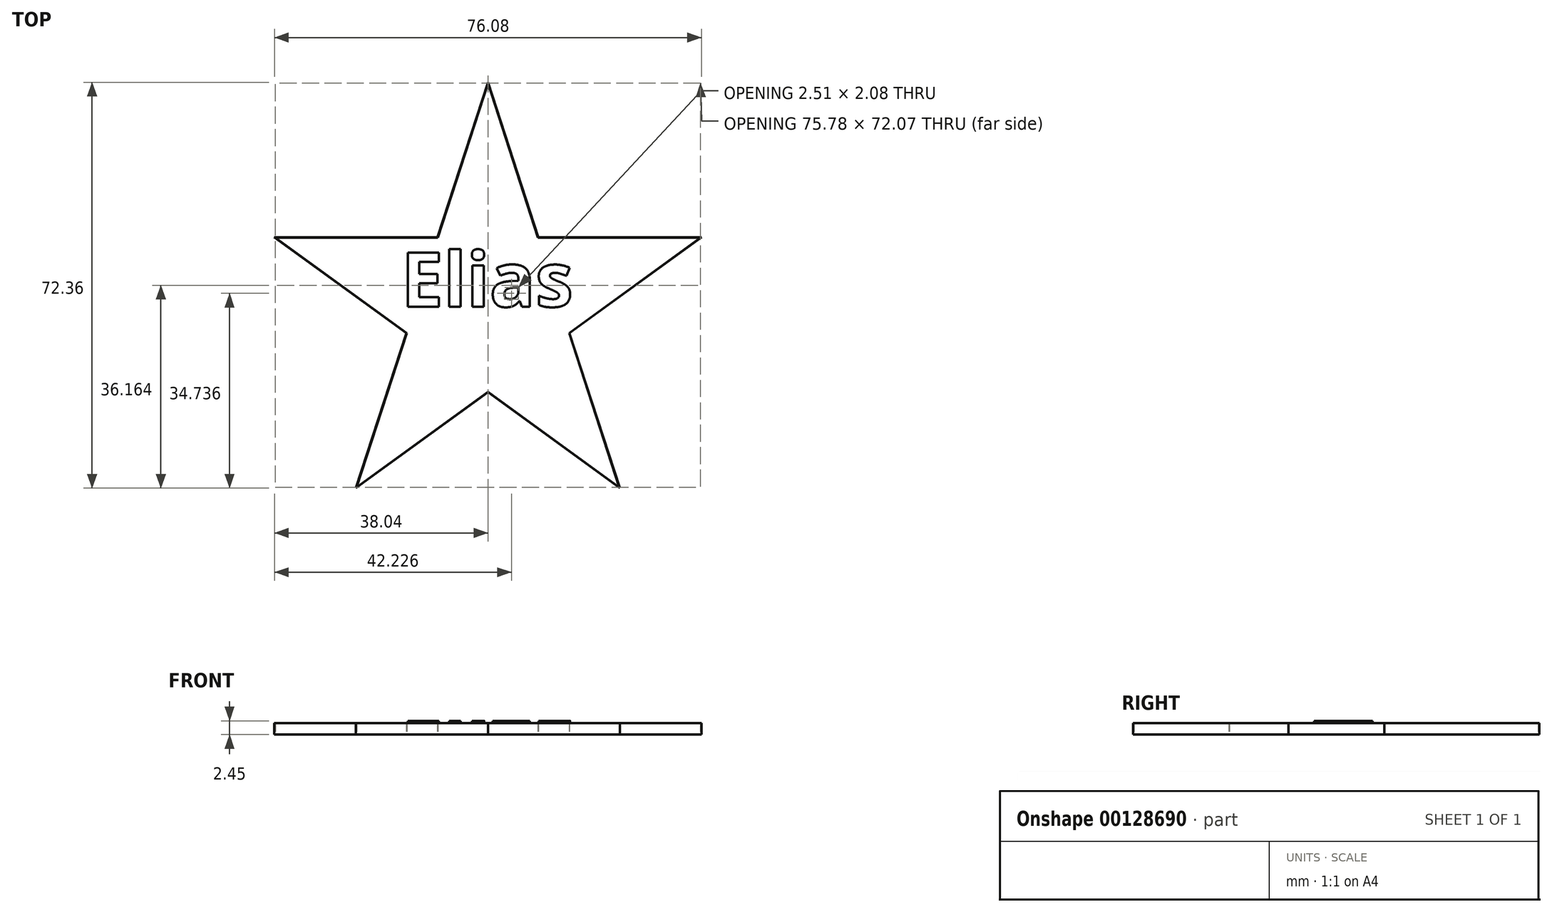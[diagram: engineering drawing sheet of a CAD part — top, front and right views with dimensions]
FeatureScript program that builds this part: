
annotation { "Feature Type Name" : "Feature", "Feature Type Description" : "" }
export const myFeature = defineFeature(function(context is Context, id is Id, definition is map)
    precondition{}
    {
        {
            assignVariable(context, id + "F0", {"name" : "Thickness", "anyValue" : 2 * mm});
        }
        {
            var Q0;
            Q0=qCreatedBy(makeId("Top.planeOp"),FACE);
            var sketch = newSketch(context, id + "F1", { "sketchPlane" : qUnion([Q0])});
            skLineSegment(sketch, "E0", {"start": v(0, 0) * mm, "end": v(0, 40) * mm, "construction": true});
            skLineSegment(sketch, "E1", {"start": v(0, 40) * mm, "end": v(-13, 0) * mm, "construction": true});
            skLineSegment(sketch, "E2", {"start": v(-13, 0) * mm, "end": v(13, 0) * mm, "construction": true});
            skLineSegment(sketch, "E3", {"start": v(0, 40) * mm, "end": v(13, 0) * mm, "construction": true});
            skPoint(sketch, "E4.center", {"position": v(0, 0) * mm});
            skLineSegment(sketch, "E5.1.0", {"start": v(-38.04, 12.36) * mm, "end": v(-4.02, -12.36) * mm, "construction": true});
            skLineSegment(sketch, "E5.1.1", {"start": v(-38.04, 12.36) * mm, "end": v(4.02, 12.36) * mm, "construction": true});
            skLineSegment(sketch, "E5.2.0", {"start": v(-23.51, -32.36) * mm, "end": v(10.51, -7.64) * mm, "construction": true});
            skLineSegment(sketch, "E5.2.1", {"start": v(-23.51, -32.36) * mm, "end": v(-10.51, 7.64) * mm, "construction": true});
            skLineSegment(sketch, "E5.3.0", {"start": v(23.51, -32.36) * mm, "end": v(10.51, 7.64) * mm, "construction": true});
            skLineSegment(sketch, "E5.3.1", {"start": v(23.51, -32.36) * mm, "end": v(-10.51, -7.64) * mm, "construction": true});
            skLineSegment(sketch, "E5.4.0", {"start": v(38.04, 12.36) * mm, "end": v(-4.02, 12.36) * mm, "construction": true});
            skLineSegment(sketch, "E5.4.1", {"start": v(38.04, 12.36) * mm, "end": v(4.02, -12.36) * mm, "construction": true});
            skPoint(sketch, "E6", {"position": v(-8.98, 12.36) * mm});
            skPoint(sketch, "E7", {"position": v(8.98, 12.36) * mm});
            skPoint(sketch, "E8", {"position": v(14.53, -4.72) * mm});
            skPoint(sketch, "E9", {"position": v(0, -15.28) * mm});
            skPoint(sketch, "E10", {"position": v(-14.53, -4.72) * mm});
            skLineSegment(sketch, "E11", {"start": v(0, 40) * mm, "end": v(8.98, 12.36) * mm});
            skLineSegment(sketch, "E12", {"start": v(38.04, 12.36) * mm, "end": v(8.98, 12.36) * mm});
            skLineSegment(sketch, "E13", {"start": v(14.53, -4.72) * mm, "end": v(38.04, 12.36) * mm});
            skLineSegment(sketch, "E14", {"start": v(14.53, -4.72) * mm, "end": v(23.51, -32.36) * mm});
            skLineSegment(sketch, "E15", {"start": v(0, -15.28) * mm, "end": v(23.51, -32.36) * mm});
            skLineSegment(sketch, "E16", {"start": v(0, -15.28) * mm, "end": v(-23.51, -32.36) * mm});
            skLineSegment(sketch, "E17", {"start": v(-14.53, -4.72) * mm, "end": v(-23.51, -32.36) * mm});
            skLineSegment(sketch, "E18", {"start": v(-14.53, -4.72) * mm, "end": v(-38.04, 12.36) * mm});
            skLineSegment(sketch, "E19", {"start": v(-38.04, 12.36) * mm, "end": v(-8.98, 12.36) * mm});
            skLineSegment(sketch, "E20", {"start": v(-8.98, 12.36) * mm, "end": v(0, 40) * mm});
            skLineSegment(sketch, "E21.0", {"start": v(-37.89, 12.31) * mm, "end": v(-8.94, 12.31) * mm});
            skLineSegment(sketch, "E21.1", {"start": v(-14.47, -4.7) * mm, "end": v(-37.89, 12.31) * mm});
            skLineSegment(sketch, "E21.2", {"start": v(-8.94, 12.31) * mm, "end": v(0, 39.84) * mm});
            skLineSegment(sketch, "E21.3", {"start": v(-14.47, -4.7) * mm, "end": v(-23.42, -32.23) * mm});
            skLineSegment(sketch, "E21.4", {"start": v(0, -15.22) * mm, "end": v(-23.42, -32.23) * mm});
            skLineSegment(sketch, "E21.5", {"start": v(0, -15.22) * mm, "end": v(23.42, -32.23) * mm});
            skLineSegment(sketch, "E21.6", {"start": v(0, 39.84) * mm, "end": v(8.94, 12.31) * mm});
            skLineSegment(sketch, "E21.7", {"start": v(37.89, 12.31) * mm, "end": v(8.94, 12.31) * mm});
            skLineSegment(sketch, "E21.8", {"start": v(14.47, -4.7) * mm, "end": v(37.89, 12.31) * mm});
            skLineSegment(sketch, "E21.9", {"start": v(14.47, -4.7) * mm, "end": v(23.42, -32.23) * mm});
            skSolve(sketch);
        }
        {
            var Q0;
            Q0=makeQuery(id+"F1.imprint","IMPRINT",FACE,{"disambiguationData":[TD([[makeQuery(id+"F1.imprint","IMPRINT",EDGE,{"derivedFrom":sQuery(id+"F1.wireOp",EDGE,"E11")}),-1.0]])]});
            extrude(context, id + "F2", {"entities" : qUnion([Q0]), "depth" : getVariable(context, 'Thickness') + 0.05 * mm});
        }
        {
            var Q0;
            Q0=makeQuery(id+"F2.opExtrude","CAP_FACE",FACE,{"disambiguationData":[OSD([sQuery(id+"F1.wireOp",EDGE,"E11"),sQuery(id+"F1.wireOp",EDGE,"E12"),sQuery(id+"F1.wireOp",EDGE,"E13"),sQuery(id+"F1.wireOp",EDGE,"E14"),sQuery(id+"F1.wireOp",EDGE,"E15"),sQuery(id+"F1.wireOp",EDGE,"E16"),sQuery(id+"F1.wireOp",EDGE,"E17"),sQuery(id+"F1.wireOp",EDGE,"E18"),sQuery(id+"F1.wireOp",EDGE,"E19"),sQuery(id+"F1.wireOp",EDGE,"E20"),sQuery(id+"F1.wireOp",EDGE,"E21.0"),sQuery(id+"F1.wireOp",EDGE,"E21.1"),sQuery(id+"F1.wireOp",EDGE,"E21.2"),sQuery(id+"F1.wireOp",EDGE,"E21.3"),sQuery(id+"F1.wireOp",EDGE,"E21.4"),sQuery(id+"F1.wireOp",EDGE,"E21.5"),sQuery(id+"F1.wireOp",EDGE,"E21.6"),sQuery(id+"F1.wireOp",EDGE,"E21.7"),sQuery(id+"F1.wireOp",EDGE,"E21.8"),sQuery(id+"F1.wireOp",EDGE,"E21.9")])],"isStart":false});
            var sketch = newSketch(context, id + "F3", { "sketchPlane" : qUnion([Q0])});
            skText(sketch, "E22", { "text": "Elias", "fontName": "OpenSans-Bold.ttf"});
            const initialGuessF3  = {"E22": [-0.0155, 0, 1, 0, 0.00972]};
            skSetInitialGuess(sketch, initialGuessF3);
            skSolve(sketch);
        }
        {
            var Q0;
            Q0 = qSketchRegion(id + "F3", true);
            extrude(context, id + "F4", {"entities" : qUnion([Q0]), "depth" : 0.4 * mm});
        }
    });
